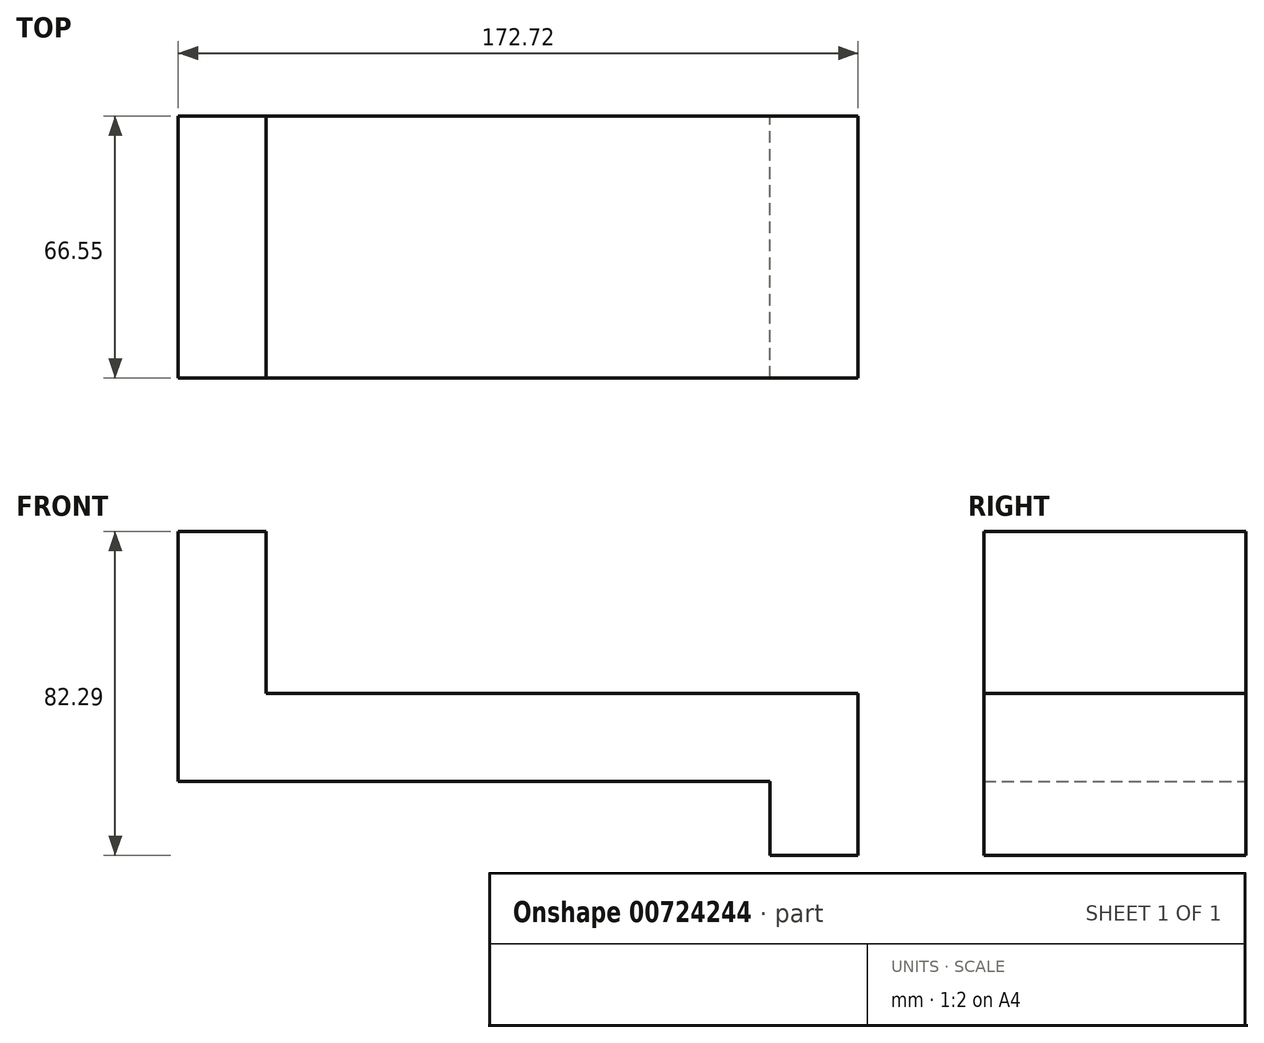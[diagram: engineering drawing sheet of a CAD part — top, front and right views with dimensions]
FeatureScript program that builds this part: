
annotation { "Feature Type Name" : "Feature", "Feature Type Description" : "" }
export const myFeature = defineFeature(function(context is Context, id is Id, definition is map)
    precondition{}
    {
        {
            var Q0;
            Q0=qCreatedBy(makeId("Front.planeOp"),FACE);
            var sketch = newSketch(context, id + "F0", { "sketchPlane" : qUnion([Q0])});
            skLineSegment(sketch, "E0", {"start": v(-99.44, 54.68) * mm, "end": v(-99.44, -8.82) * mm});
            skLineSegment(sketch, "E1", {"start": v(-99.44, -8.82) * mm, "end": v(50.93, -8.82) * mm});
            skLineSegment(sketch, "E2", {"start": v(-99.44, 54.68) * mm, "end": v(-77.09, 54.68) * mm});
            skLineSegment(sketch, "E3", {"start": v(-77.09, 54.68) * mm, "end": v(-77.09, 13.54) * mm});
            skLineSegment(sketch, "E4", {"start": v(-77.09, 13.54) * mm, "end": v(73.28, 13.54) * mm});
            skLineSegment(sketch, "E5", {"start": v(73.28, 13.54) * mm, "end": v(73.28, -27.61) * mm});
            skLineSegment(sketch, "E6", {"start": v(50.93, -8.82) * mm, "end": v(50.93, -27.61) * mm});
            skLineSegment(sketch, "E7", {"start": v(73.28, -27.61) * mm, "end": v(50.93, -27.61) * mm});
            skSolve(sketch);
        }
        {
            var Q0;
            Q0=makeQuery(id+"F0.imprint","IMPRINT",FACE,{"disambiguationData":[TD([[makeQuery(id+"F0.imprint","IMPRINT",EDGE,{"derivedFrom":sQuery(id+"F0.wireOp",EDGE,"E0")}),1.0]])]});
            extrude(context, id + "F1", {"entities" : qUnion([Q0]), "depth" : 66.55 * mm, "offsetDistance" : 25.4 * mm});
        }
    });
